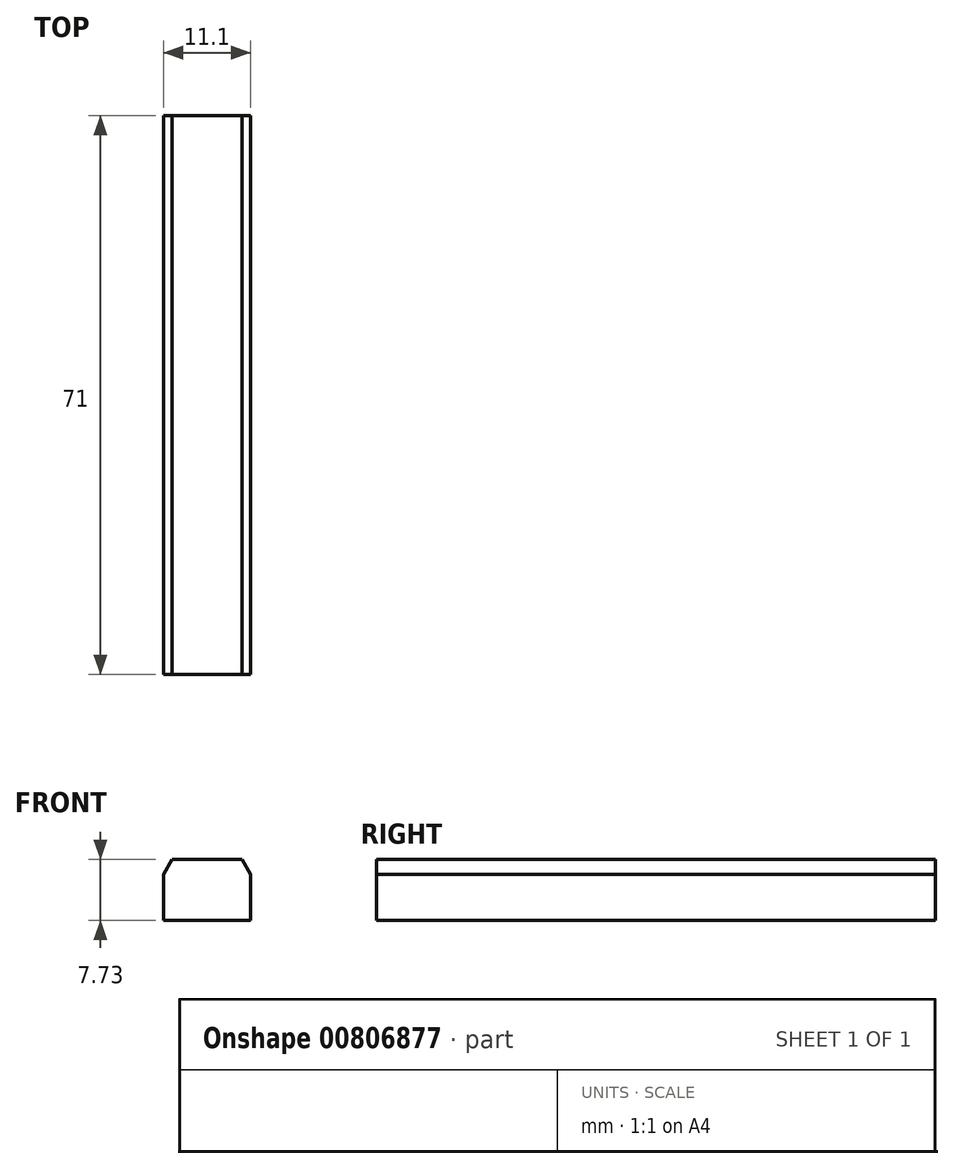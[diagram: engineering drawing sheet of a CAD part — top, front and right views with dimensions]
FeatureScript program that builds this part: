
annotation { "Feature Type Name" : "Feature", "Feature Type Description" : "" }
export const myFeature = defineFeature(function(context is Context, id is Id, definition is map)
    precondition{}
    {
        {
            var Q0;
            Q0=qCreatedBy(makeId("Front.planeOp"),FACE);
            var sketch = newSketch(context, id + "F0", { "sketchPlane" : qUnion([Q0])});
            skLineSegment(sketch, "E0.0", {"start": v(4.46, 7.7) * mm, "end": v(8.9, -0.02) * mm});
            skLineSegment(sketch, "E0.1", {"start": v(8.9, -0.02) * mm, "end": v(4.44, -7.72) * mm});
            skLineSegment(sketch, "E0.2", {"start": v(4.44, -7.72) * mm, "end": v(-4.46, -7.7) * mm});
            skLineSegment(sketch, "E0.3", {"start": v(-4.46, -7.7) * mm, "end": v(-8.9, 0.02) * mm});
            skLineSegment(sketch, "E0.4", {"start": v(-8.9, 0.02) * mm, "end": v(-4.44, 7.72) * mm});
            skLineSegment(sketch, "E0.5", {"start": v(-4.44, 7.72) * mm, "end": v(4.46, 7.7) * mm});
            skPoint(sketch, "E0.0.midPoint", {"position": v(6.68, 3.84) * mm});
            skSolve(sketch);
        }
        {
            var Q0;
            Q0=makeQuery(id+"F0.imprint","IMPRINT",FACE,{"disambiguationData":[TD([[makeQuery(id+"F0.imprint","IMPRINT",EDGE,{"derivedFrom":sQuery(id+"F0.wireOp",EDGE,"E0.0")}),-1.0]])]});
            extrude(context, id + "F1", {"entities" : qUnion([Q0]), "depth" : 71 * mm, "offsetDistance" : 25 * mm});
        }
        {
            var Q0;
            Q0=makeQuery(id+"F1.opExtrude","CAP_FACE",FACE,{"disambiguationData":[OSD([sQuery(id+"F0.wireOp",EDGE,"E0.0"),sQuery(id+"F0.wireOp",EDGE,"E0.1"),sQuery(id+"F0.wireOp",EDGE,"E0.2"),sQuery(id+"F0.wireOp",EDGE,"E0.3"),sQuery(id+"F0.wireOp",EDGE,"E0.4"),sQuery(id+"F0.wireOp",EDGE,"E0.5")])],"isStart":false});
            var sketch = newSketch(context, id + "F2", { "sketchPlane" : qUnion([Q0])});
            skLineSegment(sketch, "E1", {"start": v(-8.9, 0.02) * mm, "end": v(8.9, -0.02) * mm});
            skSolve(sketch);
        }
        {
            var Q0;
            Q0=makeQuery(id+"F2.imprint","IMPRINT",FACE,{"disambiguationData":[TD([[makeQuery(id+"F2.imprint","IMPRINT",EDGE,{"derivedFrom":sQuery(id+"F2.wireOp",EDGE,"E1")}),-1.0]])]});
            extrude(context, id + "F3", {"entities" : qUnion([Q0]), "operationType" : NewBodyOperationType.REMOVE, "oppositeDirection" : true, "depth" : 71 * mm, "offsetDistance" : 25 * mm});
        }
        {
            var Q0;
            Q0=makeQuery(id+"F1.opExtrude","CAP_FACE",FACE,{"disambiguationData":[OSD([sQuery(id+"F0.wireOp",EDGE,"E0.0"),sQuery(id+"F0.wireOp",EDGE,"E0.1"),sQuery(id+"F0.wireOp",EDGE,"E0.2"),sQuery(id+"F0.wireOp",EDGE,"E0.3"),sQuery(id+"F0.wireOp",EDGE,"E0.4"),sQuery(id+"F0.wireOp",EDGE,"E0.5")])],"isStart":true});
            var sketch = newSketch(context, id + "F4", { "sketchPlane" : qUnion([Q0])});
            skLineSegment(sketch, "E2", {"start": v(-8.9, -0.02) * mm, "end": v(-5.55, 0) * mm});
            skLineSegment(sketch, "E3", {"start": v(-5.55, 0) * mm, "end": v(-5.55, 5.81) * mm});
            skLineSegment(sketch, "E4", {"start": v(-5.55, 5.81) * mm, "end": v(-8.9, -0.02) * mm});
            skLineSegment(sketch, "E5", {"start": v(8.9, 0.02) * mm, "end": v(5.55, 0) * mm});
            skLineSegment(sketch, "E6", {"start": v(5.55, 0) * mm, "end": v(5.55, 5.8) * mm});
            skLineSegment(sketch, "E7", {"start": v(5.55, 5.8) * mm, "end": v(8.9, 0.02) * mm});
            skSolve(sketch);
        }
        {
            var Q0;
            Q0 = qSketchRegion(id + "F4", true);
            extrude(context, id + "F5", {"entities" : qUnion([Q0]), "operationType" : NewBodyOperationType.REMOVE, "oppositeDirection" : true, "depth" : 71 * mm, "offsetDistance" : 25 * mm});
        }
    });
